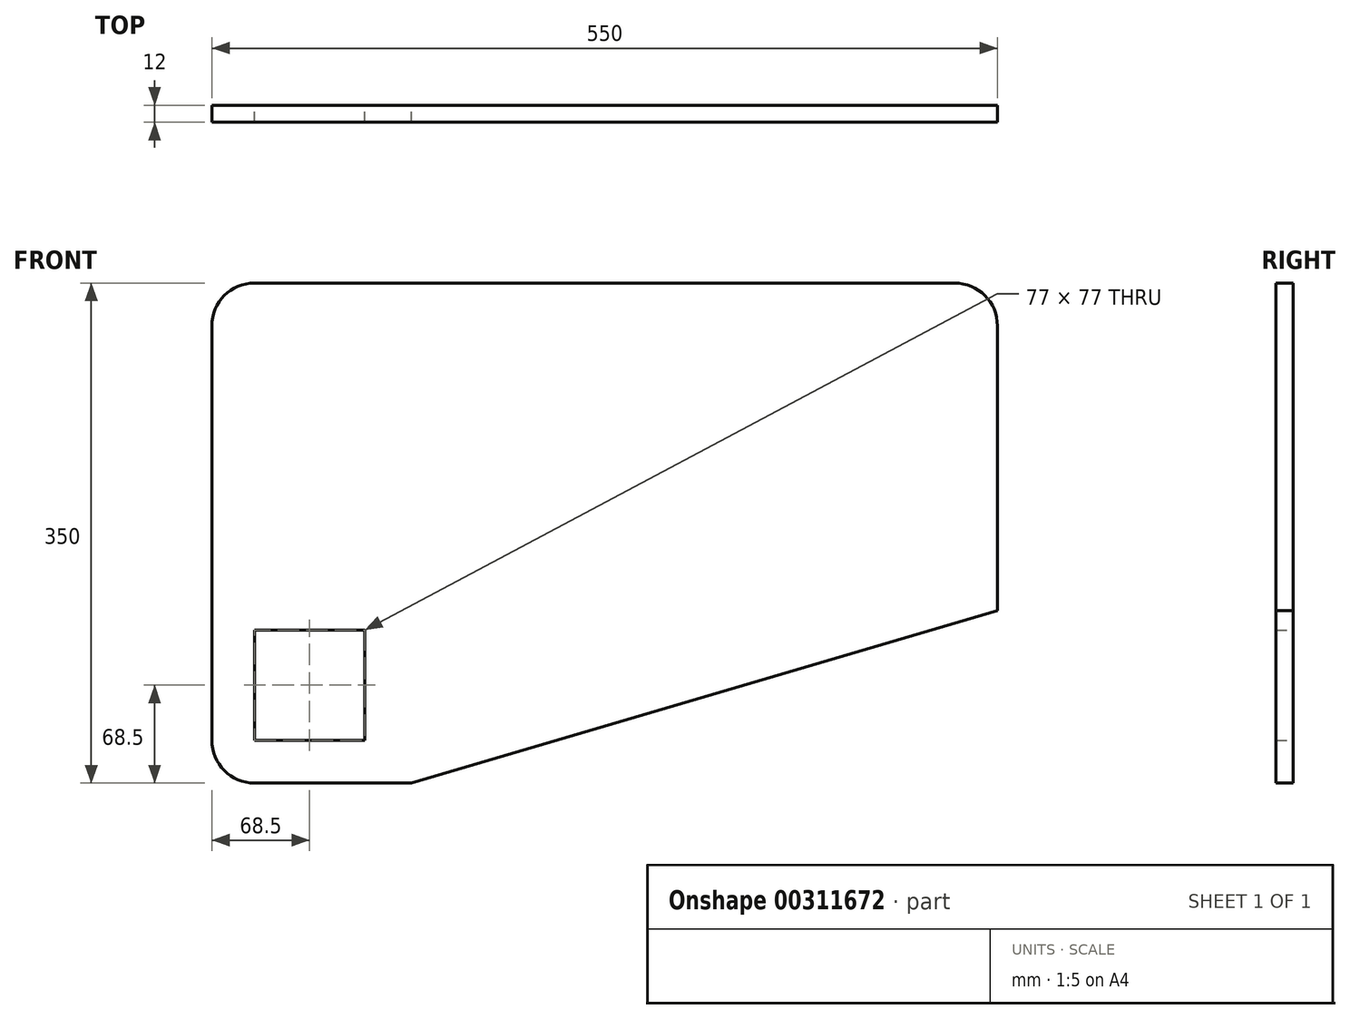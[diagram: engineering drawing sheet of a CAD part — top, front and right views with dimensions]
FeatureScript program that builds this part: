
annotation { "Feature Type Name" : "Feature", "Feature Type Description" : "" }
export const myFeature = defineFeature(function(context is Context, id is Id, definition is map)
    precondition{}
    {
        {
            var Q0;
            Q0=qCreatedBy(makeId("Front.planeOp"),FACE);
            var sketch = newSketch(context, id + "F0", { "sketchPlane" : qUnion([Q0])});
            skLineSegment(sketch, "E0.bottom", {"start": v(30, 0) * mm, "end": v(550, 0) * mm});
            skLineSegment(sketch, "E0.top", {"start": v(30, 350) * mm, "end": v(520, 350) * mm});
            skLineSegment(sketch, "E0.left", {"start": v(0, 30) * mm, "end": v(0, 320) * mm});
            skLineSegment(sketch, "E0.right", {"start": v(550, 0) * mm, "end": v(550, 320) * mm});
            skLineSegment(sketch, "E1.bottom", {"start": v(30, 30) * mm, "end": v(107, 30) * mm});
            skLineSegment(sketch, "E1.top", {"start": v(30, 107) * mm, "end": v(107, 107) * mm});
            skLineSegment(sketch, "E1.left", {"start": v(30, 30) * mm, "end": v(30, 107) * mm});
            skLineSegment(sketch, "E1.right", {"start": v(107, 30) * mm, "end": v(107, 107) * mm});
            skPoint(sketch, "E2.visualSharp", {"position": v(0, 0) * mm});
            skArc(sketch, "E2.filletArc", {"start": v(0, 30) * mm, "mid": v(8.79, 8.79) * mm, "end": v(30, 0) * mm});
            skPoint(sketch, "E3.visualSharp", {"position": v(0, 350) * mm});
            skArc(sketch, "E3.filletArc", {"start": v(30, 350) * mm, "mid": v(8.79, 341.21) * mm, "end": v(0, 320) * mm});
            skPoint(sketch, "E4.visualSharp", {"position": v(550, 350) * mm});
            skArc(sketch, "E4.filletArc", {"start": v(550, 320) * mm, "mid": v(541.21, 341.21) * mm, "end": v(520, 350) * mm});
            skLineSegment(sketch, "E5", {"start": v(550, 120.82) * mm, "end": v(139.87, 0) * mm});
            skSolve(sketch);
        }
        {
            var Q0;
            Q0=makeQuery(id+"F0.imprint","IMPRINT",FACE,{"disambiguationData":[TD([[makeQuery(id+"F0.imprint","IMPRINT",EDGE,{"derivedFrom":sQuery(id+"F0.wireOp",EDGE,"E0.top")}),-1.0]])]});
            extrude(context, id + "F1", {"entities" : qUnion([Q0]), "depth" : 12 * mm, "offsetDistance" : 25 * mm});
        }
    });
